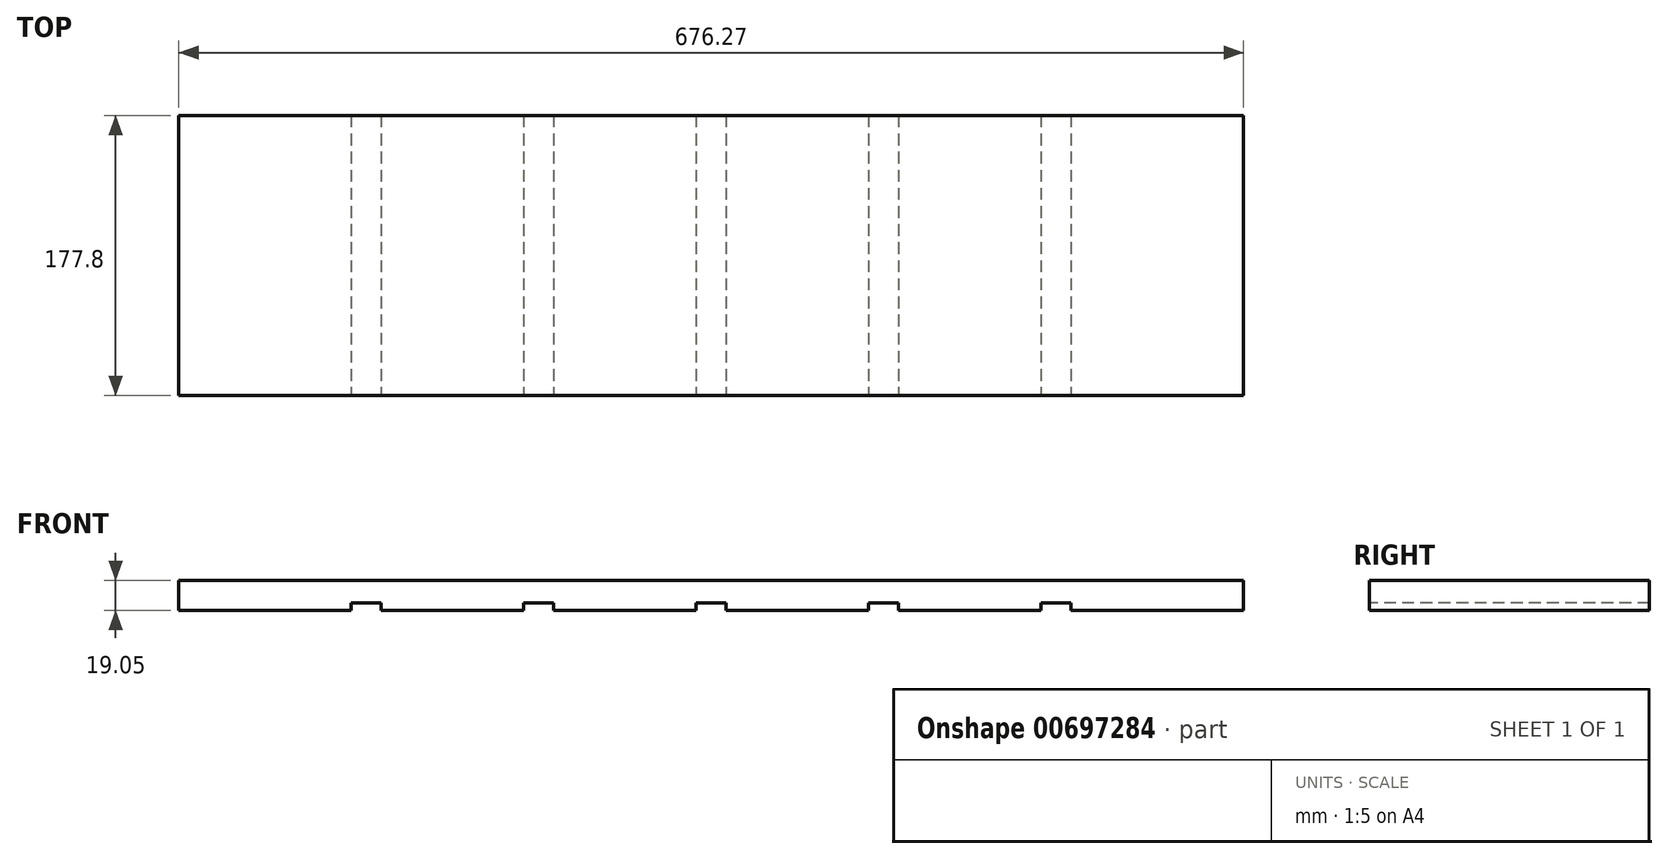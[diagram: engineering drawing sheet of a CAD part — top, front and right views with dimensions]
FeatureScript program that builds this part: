
annotation { "Feature Type Name" : "Feature", "Feature Type Description" : "" }
export const myFeature = defineFeature(function(context is Context, id is Id, definition is map)
    precondition{}
    {
        {
            var Q0;
            Q0=qCreatedBy(makeId("Front.planeOp"),FACE);
            var sketch = newSketch(context, id + "F0", { "sketchPlane" : qUnion([Q0])});
            skLineSegment(sketch, "E0.bottom", {"start": v(0, 0) * mm, "end": v(676.28, 0) * mm});
            skLineSegment(sketch, "E0.top", {"start": v(0, 19.05) * mm, "end": v(676.28, 19.05) * mm});
            skLineSegment(sketch, "E0.left", {"start": v(0, 0) * mm, "end": v(0, 19.05) * mm});
            skLineSegment(sketch, "E0.right", {"start": v(676.28, 0) * mm, "end": v(676.28, 19.05) * mm});
            skSolve(sketch);
        }
        {
            var Q0;
            Q0=qCreatedBy(makeId("Front.planeOp"),FACE);
            var sketch = newSketch(context, id + "F1", { "sketchPlane" : qUnion([Q0])});
            skLineSegment(sketch, "E1.bottom", {"start": v(109.54, 0) * mm, "end": v(128.59, 0) * mm});
            skLineSegment(sketch, "E1.top", {"start": v(109.54, 4.76) * mm, "end": v(128.59, 4.76) * mm});
            skLineSegment(sketch, "E1.left", {"start": v(109.54, 0) * mm, "end": v(109.54, 4.76) * mm});
            skLineSegment(sketch, "E1.right", {"start": v(128.59, 0) * mm, "end": v(128.59, 4.76) * mm});
            skLineSegment(sketch, "E2.bottom", {"start": v(219.08, 0) * mm, "end": v(238.13, 0) * mm});
            skLineSegment(sketch, "E2.top", {"start": v(219.08, 4.76) * mm, "end": v(238.13, 4.76) * mm});
            skLineSegment(sketch, "E2.left", {"start": v(219.08, 0) * mm, "end": v(219.08, 4.76) * mm});
            skLineSegment(sketch, "E2.right", {"start": v(238.13, 0) * mm, "end": v(238.13, 4.76) * mm});
            skLineSegment(sketch, "E3.bottom", {"start": v(328.61, 0) * mm, "end": v(347.66, 0) * mm});
            skLineSegment(sketch, "E3.top", {"start": v(328.61, 4.76) * mm, "end": v(347.66, 4.76) * mm});
            skLineSegment(sketch, "E3.left", {"start": v(328.61, 0) * mm, "end": v(328.61, 4.76) * mm});
            skLineSegment(sketch, "E3.right", {"start": v(347.66, 0) * mm, "end": v(347.66, 4.76) * mm});
            skLineSegment(sketch, "E4.bottom", {"start": v(438.15, 0) * mm, "end": v(457.2, 0) * mm});
            skLineSegment(sketch, "E4.top", {"start": v(438.15, 4.76) * mm, "end": v(457.2, 4.76) * mm});
            skLineSegment(sketch, "E4.left", {"start": v(438.15, 0) * mm, "end": v(438.15, 4.76) * mm});
            skLineSegment(sketch, "E4.right", {"start": v(457.2, 0) * mm, "end": v(457.2, 4.76) * mm});
            skLineSegment(sketch, "E5.bottom", {"start": v(547.69, 0) * mm, "end": v(566.74, 0) * mm});
            skLineSegment(sketch, "E5.top", {"start": v(547.69, 4.76) * mm, "end": v(566.74, 4.76) * mm});
            skLineSegment(sketch, "E5.left", {"start": v(547.69, 0) * mm, "end": v(547.69, 4.76) * mm});
            skLineSegment(sketch, "E5.right", {"start": v(566.74, 0) * mm, "end": v(566.74, 4.76) * mm});
            skSolve(sketch);
        }
        {
            var Q0;
            Q0 = qSketchRegion(id + "F0", true);
            extrude(context, id + "F2", {"entities" : qUnion([Q0]), "oppositeDirection" : true, "depth" : 177.8 * mm, "offsetDistance" : 25.4 * mm});
        }
        {
            var Q0;
            Q0 = qSketchRegion(id + "F1", true);
            extrude(context, id + "F3", {"entities" : qUnion([Q0]), "operationType" : NewBodyOperationType.REMOVE, "endBound" : BoundingType.THROUGH_ALL, "oppositeDirection" : true, "depth" : 25.4 * mm, "offsetDistance" : 25.4 * mm});
        }
    });
